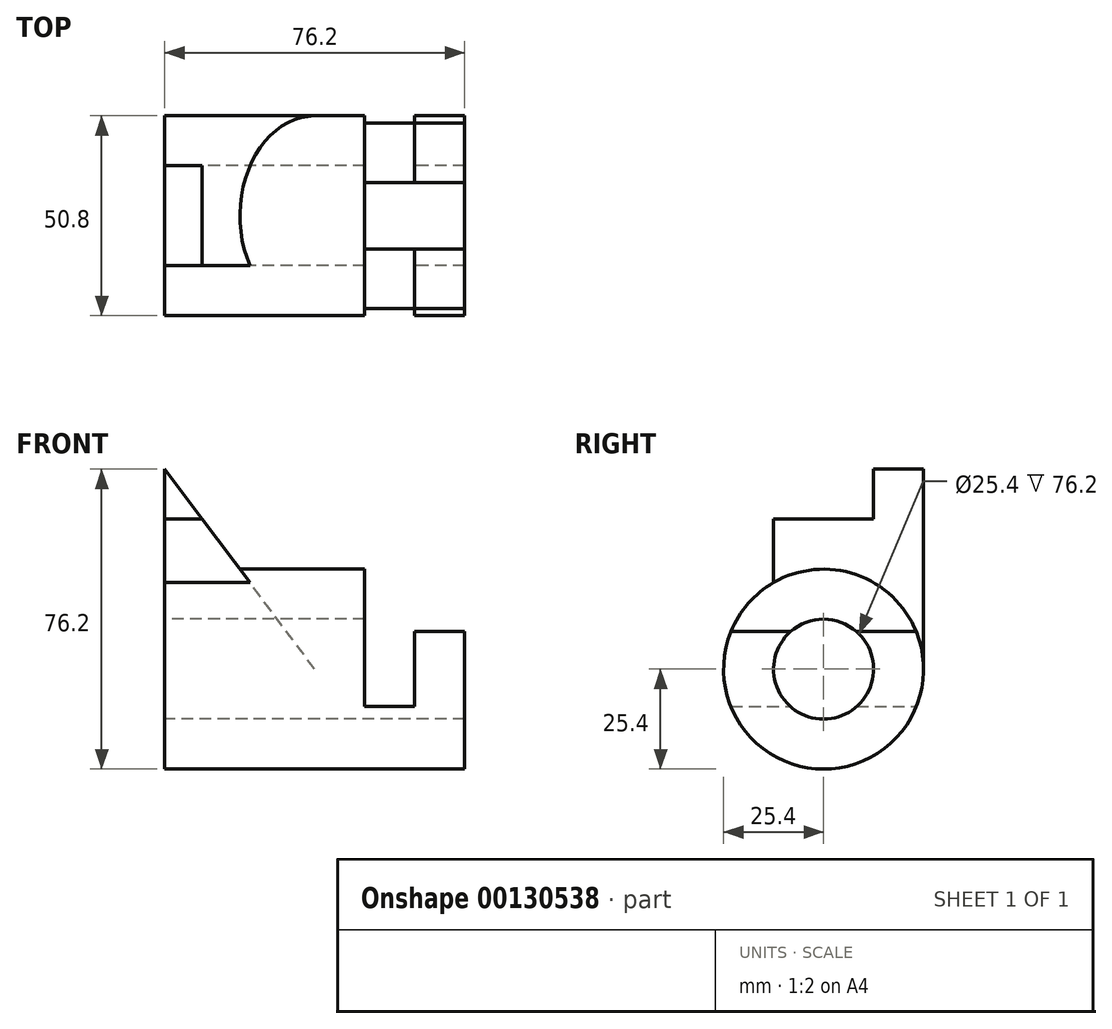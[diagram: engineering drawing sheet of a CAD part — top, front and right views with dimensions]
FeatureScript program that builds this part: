
annotation { "Feature Type Name" : "Feature", "Feature Type Description" : "" }
export const myFeature = defineFeature(function(context is Context, id is Id, definition is map)
    precondition{}
    {
        {
            var Q0;
            Q0=qCreatedBy(makeId("Right.planeOp"),FACE);
            var sketch = newSketch(context, id + "F0", { "sketchPlane" : qUnion([Q0])});
            skCircle(sketch, "E0", {"center": v(0, 0) * mm, "radius": 12.7 * mm});
            skCircle(sketch, "E1", {"center": v(0, 0) * mm, "radius": 25.4 * mm});
            skSolve(sketch);
        }
        {
            var Q0;
            Q0 = qSketchRegion(id + "F0", true);
            extrude(context, id + "F1", {"entities" : qUnion([Q0]), "depth" : 50.8 * mm});
        }
        {
            var Q0;
            Q0=makeQuery(id+"F1.opExtrude","CAP_FACE",FACE,{"disambiguationData":[OSD([sQuery(id+"F0.wireOp",EDGE,"E0"),sQuery(id+"F0.wireOp",EDGE,"E1")])],"isStart":false});
            var sketch = newSketch(context, id + "F2", { "sketchPlane" : qUnion([Q0])});
            skLineSegment(sketch, "E2", {"start": v(-23.55, -9.53) * mm, "end": v(-8.4, -9.53) * mm});
            skArc(sketch, "E3", {"start": v(23.55, -9.53) * mm, "mid": v(0, -25.4) * mm, "end": v(-23.55, -9.52) * mm});
            skArc(sketch, "E4", {"start": v(8.4, -9.53) * mm, "mid": v(0, -12.7) * mm, "end": v(-8.4, -9.53) * mm});
            skLineSegment(sketch, "E5.trimOffspring", {"start": v(8.4, -9.53) * mm, "end": v(23.55, -9.53) * mm});
            skSolve(sketch);
        }
        {
            var Q0;
            Q0 = qSketchRegion(id + "F2", true);
            extrude(context, id + "F3", {"entities" : qUnion([Q0]), "operationType" : NewBodyOperationType.ADD, "depth" : 12.7 * mm});
        }
        {
            var Q0;
            Q0=makeQuery(id+"F3.opExtrude","CAP_FACE",FACE,{"disambiguationData":[OSD([sQuery(id+"F2.wireOp",EDGE,"E2"),sQuery(id+"F2.wireOp",EDGE,"E3"),sQuery(id+"F2.wireOp",EDGE,"E4"),sQuery(id+"F2.wireOp",EDGE,"E5.trimOffspring")])],"isStart":false});
            var sketch = newSketch(context, id + "F4", { "sketchPlane" : qUnion([Q0])});
            skArc(sketch, "E6.0", {"start": v(23.55, -9.52) * mm, "mid": v(25.4, 0) * mm, "end": v(23.55, 9.53) * mm});
            skArc(sketch, "E7.0", {"start": v(8.4, -9.53) * mm, "mid": v(12.7, 0) * mm, "end": v(8.4, 9.53) * mm});
            skLineSegment(sketch, "E8", {"start": v(-23.55, 9.53) * mm, "end": v(-8.4, 9.53) * mm});
            skArc(sketch, "E9", {"start": v(-23.55, 9.52) * mm, "mid": v(0, -25.4) * mm, "end": v(23.55, 9.52) * mm});
            skArc(sketch, "E10", {"start": v(-8.4, 9.52) * mm, "mid": v(0, -12.7) * mm, "end": v(8.4, 9.53) * mm});
            skLineSegment(sketch, "E11.trimOffspring", {"start": v(8.4, 9.53) * mm, "end": v(23.55, 9.53) * mm});
            skArc(sketch, "E12.trimOffspring", {"start": v(-23.55, 9.52) * mm, "mid": v(-25.4, 0) * mm, "end": v(-23.55, -9.52) * mm});
            skArc(sketch, "E13.trimOffspring", {"start": v(-8.4, 9.52) * mm, "mid": v(-12.7, 0) * mm, "end": v(-8.4, -9.53) * mm});
            skSolve(sketch);
        }
        {
            var Q0;
            Q0 = qSketchRegion(id + "F4", true);
            extrude(context, id + "F5", {"entities" : qUnion([Q0]), "operationType" : NewBodyOperationType.ADD, "depth" : 12.7 * mm});
        }
        {
            var Q0;
            Q0=qCreatedBy(makeId("Front.planeOp"),FACE);
            cPlane(context, id + "F6", {"entities" : qUnion([Q0]), "cplaneType" : CPlaneType.OFFSET, "offset" : 12.7 * mm, "width" : 152.4 * mm, "height" : 152.4 * mm});
        }
        {
            var Q0;
            Q0=qCreatedBy(id+"F6.planeOp",FACE);
            var sketch = newSketch(context, id + "F7", { "sketchPlane" : qUnion([Q0])});
            skLineSegment(sketch, "E14", {"start": v(0, 0) * mm, "end": v(0, 50.8) * mm});
            skLineSegment(sketch, "E15", {"start": v(0, 0) * mm, "end": v(76.2, 0) * mm, "construction": true});
            skPoint(sketch, "E16", {"position": v(38.1, 0) * mm});
            skLineSegment(sketch, "E17", {"start": v(38.1, 0) * mm, "end": v(0, 50.8) * mm, "construction": true});
            skPoint(sketch, "E18", {"position": v(19.05, 25.4) * mm});
            skLineSegment(sketch, "E19", {"start": v(19.05, 25.4) * mm, "end": v(0, 50.8) * mm});
            skLineSegment(sketch, "E20", {"start": v(19.05, 25.4) * mm, "end": v(0, 25.4) * mm});
            skLineSegment(sketch, "E21", {"start": v(0, 38.1) * mm, "end": v(9.52, 38.1) * mm});
            skLineSegment(sketch, "E22", {"start": v(0, 19.05) * mm, "end": v(23.81, 19.05) * mm});
            skLineSegment(sketch, "E23", {"start": v(19.05, 25.4) * mm, "end": v(23.81, 19.05) * mm});
            skSolve(sketch);
        }
        {
            var Q0;
            {var subQ0=sQuery(id+"F7.wireOp",EDGE,"E20");Q0=makeQuery(id+"F7.imprint","IMPRINT",FACE,{"disambiguationData":[TD([[makeQuery(id+"F7.imprint","IMPRINT",EDGE,{"derivedFrom":subQ0}),-1.0]])]});}
            var Q1;
            {var subQ0=sQuery(id+"F7.wireOp",EDGE,"E20");Q1=makeQuery(id+"F7.imprint","IMPRINT",FACE,{"disambiguationData":[TD([[makeQuery(id+"F7.imprint","IMPRINT",EDGE,{"derivedFrom":subQ0}),1.0]])]});}
            extrude(context, id + "F8", {"entities" : qUnion([Q0, Q1]), "operationType" : NewBodyOperationType.ADD, "oppositeDirection" : true, "depth" : 25.4 * mm});
        }
        {
            var Q0;
            Q0=makeQuery(id+"F8.opExtrude","CAP_FACE",FACE,{"disambiguationData":[OSD([sQuery(id+"F7.wireOp",EDGE,"E14"),sQuery(id+"F7.wireOp",EDGE,"E19"),sQuery(id+"F7.wireOp",EDGE,"E21"),sQuery(id+"F7.wireOp",EDGE,"E22"),sQuery(id+"F7.wireOp",EDGE,"E23")])],"isStart":false});
            var sketch = newSketch(context, id + "F9", { "sketchPlane" : qUnion([Q0])});
            skLineSegment(sketch, "E24.0", {"start": v(0, 0) * mm, "end": v(0, 50.8) * mm});
            skLineSegment(sketch, "E24.1", {"start": v(-19.05, 25.4) * mm, "end": v(0, 50.8) * mm});
            skLineSegment(sketch, "E24.2", {"start": v(-38.1, 0) * mm, "end": v(0, 50.8) * mm});
            skLineSegment(sketch, "E24.3", {"start": v(0, 0) * mm, "end": v(-76.2, 0) * mm});
            skSolve(sketch);
        }
        {
            var Q0;
            Q0 = qSketchRegion(id + "F9", true);
            extrude(context, id + "F10", {"entities" : qUnion([Q0]), "operationType" : NewBodyOperationType.ADD, "depth" : 12.7 * mm});
        }
    });
